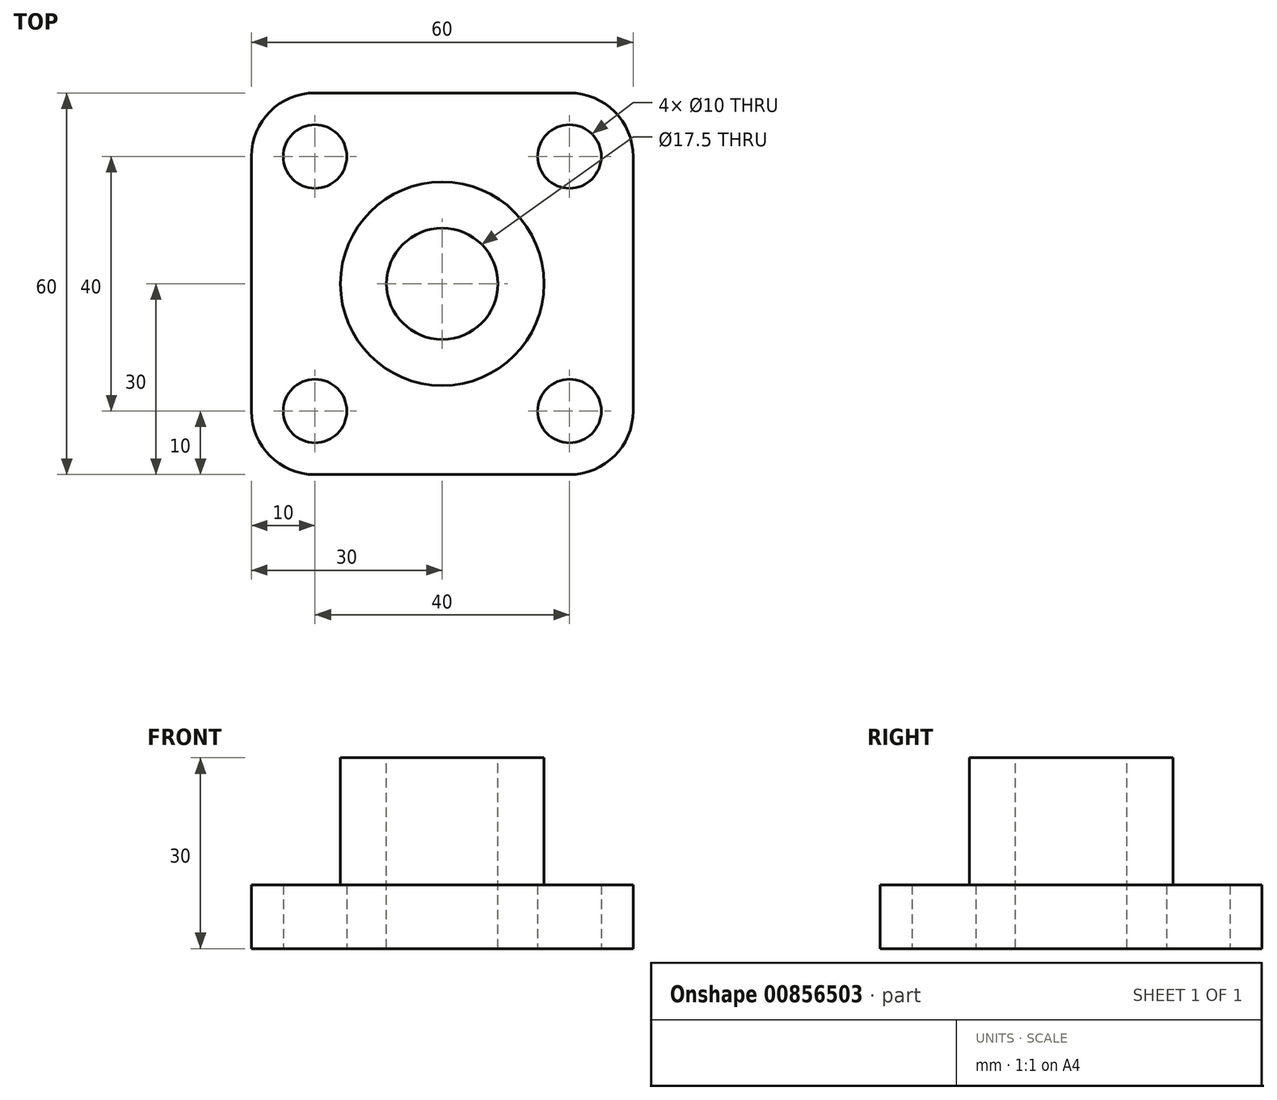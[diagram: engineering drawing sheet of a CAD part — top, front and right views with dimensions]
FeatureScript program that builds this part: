
annotation { "Feature Type Name" : "Feature", "Feature Type Description" : "" }
export const myFeature = defineFeature(function(context is Context, id is Id, definition is map)
    precondition{}
    {
        {
            var Q0;
            Q0=qCreatedBy(makeId("Top.planeOp"),FACE);
            var sketch = newSketch(context, id + "F0", { "sketchPlane" : qUnion([Q0])});
            skLineSegment(sketch, "E0.bottom", {"start": v(-30, 30) * mm, "end": v(30, 30) * mm});
            skLineSegment(sketch, "E0.top", {"start": v(-30, -30) * mm, "end": v(30, -30) * mm});
            skLineSegment(sketch, "E0.left", {"start": v(-30, 30) * mm, "end": v(-30, -30) * mm});
            skLineSegment(sketch, "E0.right", {"start": v(30, 30) * mm, "end": v(30, -30) * mm});
            skPoint(sketch, "E0.middle", {"position": v(0, 0) * mm});
            skLineSegment(sketch, "E1.bottom", {"start": v(-20, 20) * mm, "end": v(20, 20) * mm});
            skLineSegment(sketch, "E1.top", {"start": v(-20, -20) * mm, "end": v(20, -20) * mm});
            skLineSegment(sketch, "E1.left", {"start": v(-20, 20) * mm, "end": v(-20, -20) * mm});
            skLineSegment(sketch, "E1.right", {"start": v(20, 20) * mm, "end": v(20, -20) * mm});
            skPoint(sketch, "E2", {"position": v(-20, -20) * mm});
            skPoint(sketch, "E3", {"position": v(-20, 20) * mm});
            skPoint(sketch, "E4", {"position": v(20, 20) * mm});
            skPoint(sketch, "E5", {"position": v(20, -20) * mm});
            skCircle(sketch, "E6", {"center": v(0, 0) * mm, "radius": 16 * mm});
            skSolve(sketch);
        }
        {
            var Q0;
            Q0=makeQuery(id+"F0.imprint","IMPRINT",FACE,{"disambiguationData":[TD([[makeQuery(id+"F0.imprint","IMPRINT",EDGE,{"derivedFrom":sQuery(id+"F0.wireOp",EDGE,"E0.bottom")}),-1.0]])]});
            var Q1;
            Q1=makeQuery(id+"F0.imprint","IMPRINT",FACE,{"disambiguationData":[TD([[makeQuery(id+"F0.imprint","IMPRINT",EDGE,{"derivedFrom":sQuery(id+"F0.wireOp",EDGE,"E1.bottom")}),-1.0]])]});
            var Q2;
            Q2=makeQuery(id+"F0.imprint","IMPRINT",FACE,{"disambiguationData":[TD([[makeQuery(id+"F0.imprint","IMPRINT",EDGE,{"derivedFrom":sQuery(id+"F0.wireOp",EDGE,"E6")}),1.0]])]});
            extrude(context, id + "F1", {"entities" : qUnion([Q0, Q1, Q2]), "depth" : 10 * mm, "offsetDistance" : 25 * mm});
        }
        {
            var Q0;
            Q0=makeQuery(id+"F1.opExtrude","SWEPT_EDGE",EDGE,{"disambiguationData":[OSD([sQuery(id+"F0.wireOp",EDGE,"E0.top"),sQuery(id+"F0.wireOp",EDGE,"E0.left")])]});
            var Q1;
            Q1=makeQuery(id+"F1.opExtrude","SWEPT_EDGE",EDGE,{"disambiguationData":[OSD([sQuery(id+"F0.wireOp",EDGE,"E0.top"),sQuery(id+"F0.wireOp",EDGE,"E0.right")])]});
            var Q2;
            Q2=makeQuery(id+"F1.opExtrude","SWEPT_EDGE",EDGE,{"disambiguationData":[OSD([sQuery(id+"F0.wireOp",EDGE,"E0.bottom"),sQuery(id+"F0.wireOp",EDGE,"E0.right")])]});
            var Q3;
            Q3=makeQuery(id+"F1.opExtrude","SWEPT_EDGE",EDGE,{"disambiguationData":[OSD([sQuery(id+"F0.wireOp",EDGE,"E0.bottom"),sQuery(id+"F0.wireOp",EDGE,"E0.left")])]});
            fillet(context, id + "F2", {"entities" : qUnion([Q0, Q1, Q2, Q3]), "radius" : 10 * mm, "tangentPropagation" : true, "allowEdgeOverflow" : false});
        }
        {
            var Q0;
            Q0=sQuery(id+"F0.wireOp",VERTEX,"E5");
            var Q1;
            Q1=sQuery(id+"F0.wireOp",VERTEX,"E2");
            var Q2;
            Q2=sQuery(id+"F0.wireOp",VERTEX,"E3");
            var Q3;
            Q3=sQuery(id+"F0.wireOp",VERTEX,"E4");
            var Q4;
            Q4=makeQuery(id+"F1.opExtrude","SWEPT_BODY",BODY,{"disambiguationData":[OSD([sQuery(id+"F0.wireOp",EDGE,"E0.bottom"),sQuery(id+"F0.wireOp",EDGE,"E0.top"),sQuery(id+"F0.wireOp",EDGE,"E0.left"),sQuery(id+"F0.wireOp",EDGE,"E0.right")])]});
            hole(context, id + "F3", {"style" : HoleStyle.SIMPLE, "endStyle" : HoleEndStyle.BLIND, "oppositeDirection" : true, "holeDiameter" : 10 * mm, "majorDiameter" : 5 * mm, "holeDepth" : 10 * mm, "isTappedThrough" : true, "tappedDepth" : 12 * mm, "tapClearance" : 3, "locations" : qUnion([Q0, Q1, Q2, Q3]), "scope" : qUnion([Q4])});
        }
        {
            var Q0;
            Q0=makeQuery(id+"F0.imprint","IMPRINT",FACE,{"disambiguationData":[TD([[makeQuery(id+"F0.imprint","IMPRINT",EDGE,{"derivedFrom":sQuery(id+"F0.wireOp",EDGE,"E6")}),1.0]])]});
            extrude(context, id + "F4", {"entities" : qUnion([Q0]), "operationType" : NewBodyOperationType.ADD, "depth" : 30 * mm, "offsetDistance" : 25 * mm});
        }
        {
            var Q0;
            Q0=makeQuery(id+"F4.opExtrude","CAP_FACE",FACE,{"disambiguationData":[OSD([sQuery(id+"F0.wireOp",EDGE,"E6")])],"isStart":false});
            var sketch = newSketch(context, id + "F5", { "sketchPlane" : qUnion([Q0])});
            skPoint(sketch, "E7", {"position": v(0, 0) * mm});
            skSolve(sketch);
        }
        {
            var Q0;
            Q0=sQuery(id+"F5.wireOp",VERTEX,"E7");
            var Q1;
            Q1=makeQuery(id+"F1.opExtrude","SWEPT_BODY",BODY,{"disambiguationData":[OSD([sQuery(id+"F0.wireOp",EDGE,"E0.bottom"),sQuery(id+"F0.wireOp",EDGE,"E0.top"),sQuery(id+"F0.wireOp",EDGE,"E0.left"),sQuery(id+"F0.wireOp",EDGE,"E0.right")])]});
            hole(context, id + "F6", {"style" : HoleStyle.SIMPLE, "endStyle" : HoleEndStyle.BLIND, "standardTappedOrClearance" : lookupTablePath({ "fit" : "Normal", "standard" : "ISO", "size" : "M16", "type" : "Clearance" }), "standardBlindInLast" : lookupTablePath({ "fit" : "Standard", "standard" : "ISO", "size" : "M16", "type" : "Clearance" }), "holeDiameter" : 17.5 * mm, "majorDiameter" : 5 * mm, "holeDepth" : 30 * mm, "isTappedThrough" : true, "tappedDepth" : 12 * mm, "tapClearance" : 3, "locations" : qUnion([Q0]), "scope" : qUnion([Q1])});
        }
    });
